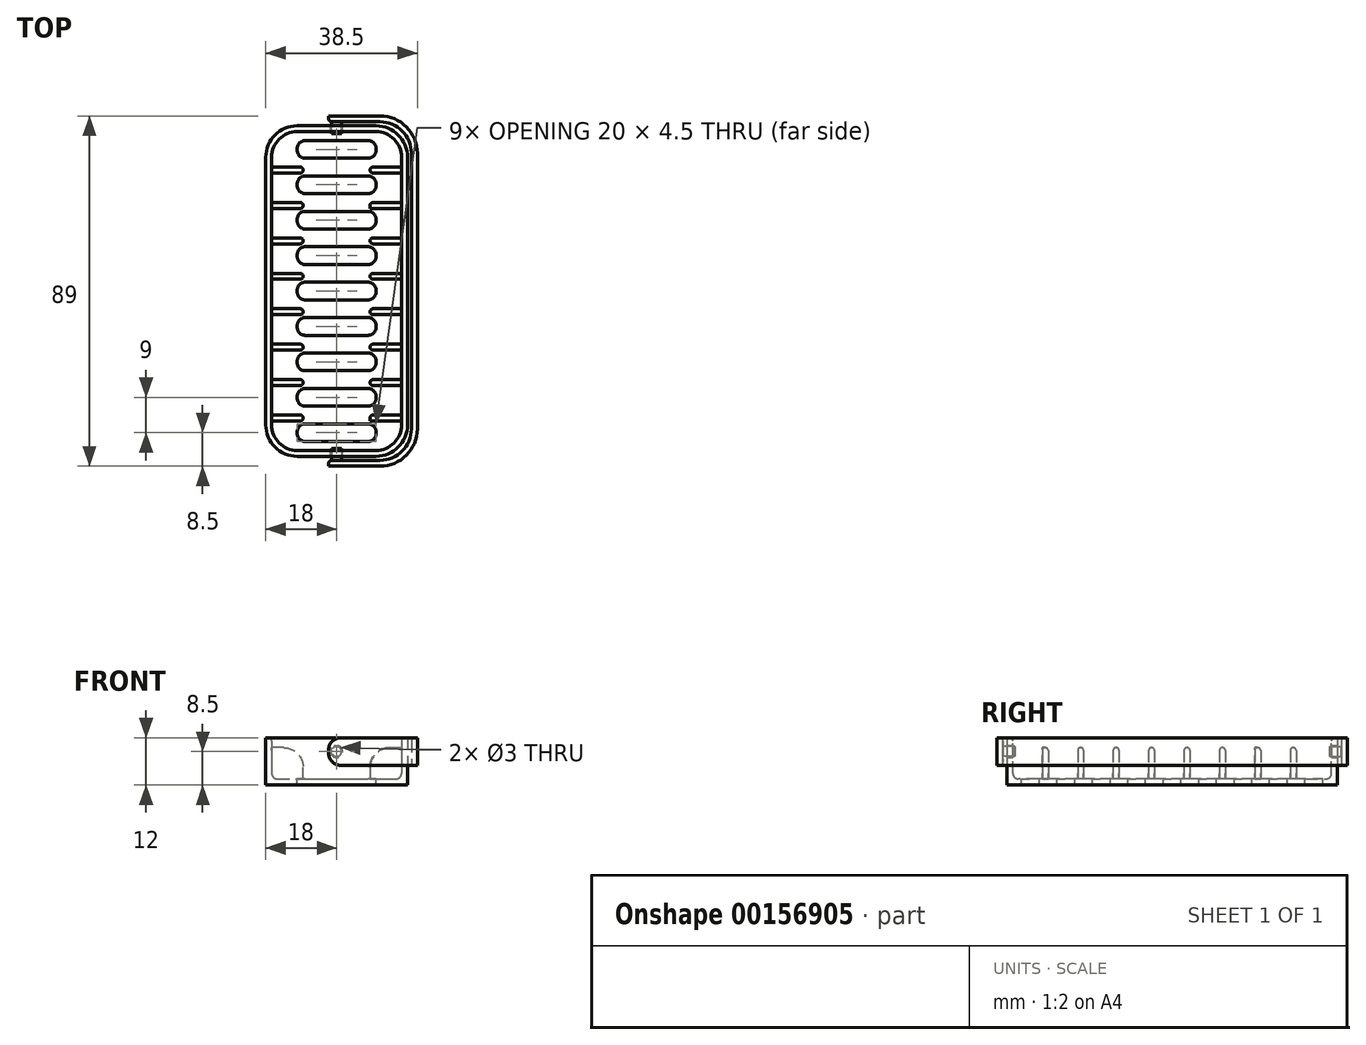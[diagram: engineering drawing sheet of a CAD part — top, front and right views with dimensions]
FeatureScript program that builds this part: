
annotation { "Feature Type Name" : "Feature", "Feature Type Description" : "" }
export const myFeature = defineFeature(function(context is Context, id is Id, definition is map)
    precondition{}
    {
        {
            var Q0;
            Q0=qCreatedBy(makeId("Top.planeOp"),FACE);
            var sketch = newSketch(context, id + "F0", { "sketchPlane" : qUnion([Q0])});
            skLineSegment(sketch, "E0.bottom", {"start": v(-18, 42) * mm, "end": v(18, 42) * mm});
            skLineSegment(sketch, "E0.top", {"start": v(-18, -42) * mm, "end": v(18, -42) * mm});
            skLineSegment(sketch, "E0.left", {"start": v(-18, 42) * mm, "end": v(-18, -42) * mm});
            skLineSegment(sketch, "E0.right", {"start": v(18, 42) * mm, "end": v(18, -42) * mm});
            skLineSegment(sketch, "E1", {"start": v(-18, 0) * mm, "end": v(18, 0) * mm, "construction": true});
            skSolve(sketch);
        }
        {
            var Q0;
            Q0=makeQuery(id+"F0.imprint","IMPRINT",FACE,{"disambiguationData":[TD([[makeQuery(id+"F0.imprint","IMPRINT",EDGE,{"derivedFrom":sQuery(id+"F0.wireOp",EDGE,"E0.bottom")}),-1.0]])]});
            extrude(context, id + "F1", {"entities" : qUnion([Q0]), "depth" : 12 * mm});
        }
        {
            var Q0;
            Q0=makeQuery(id+"F1.opExtrude","SWEPT_EDGE",EDGE,{"disambiguationData":[OSD([sQuery(id+"F0.wireOp",EDGE,"E0.bottom"),sQuery(id+"F0.wireOp",EDGE,"E0.right")])]});
            var Q1;
            Q1=makeQuery(id+"F1.opExtrude","SWEPT_EDGE",EDGE,{"disambiguationData":[OSD([sQuery(id+"F0.wireOp",EDGE,"E0.top"),sQuery(id+"F0.wireOp",EDGE,"E0.right")])]});
            var Q2;
            Q2=makeQuery(id+"F1.opExtrude","SWEPT_EDGE",EDGE,{"disambiguationData":[OSD([sQuery(id+"F0.wireOp",EDGE,"E0.top"),sQuery(id+"F0.wireOp",EDGE,"E0.left")])]});
            var Q3;
            Q3=makeQuery(id+"F1.opExtrude","SWEPT_EDGE",EDGE,{"disambiguationData":[OSD([sQuery(id+"F0.wireOp",EDGE,"E0.bottom"),sQuery(id+"F0.wireOp",EDGE,"E0.left")])]});
            fillet(context, id + "F2", {"entities" : qUnion([Q0, Q1, Q2, Q3]), "radius" : 8 * mm, "tangentPropagation" : true, "allowEdgeOverflow" : false});
        }
        {
            var Q0;
            Q0=makeQuery(id+"F1.opExtrude","CAP_FACE",FACE,{"disambiguationData":[OSD([sQuery(id+"F0.wireOp",EDGE,"E0.bottom"),sQuery(id+"F0.wireOp",EDGE,"E0.top"),sQuery(id+"F0.wireOp",EDGE,"E0.left"),sQuery(id+"F0.wireOp",EDGE,"E0.right")])],"isStart":false});
            var Q1;
            Q1=makeQuery(id+"F1.opExtrude","CAP_FACE",FACE,{"disambiguationData":[OSD([sQuery(id+"F0.wireOp",EDGE,"E0.bottom"),sQuery(id+"F0.wireOp",EDGE,"E0.top"),sQuery(id+"F0.wireOp",EDGE,"E0.left"),sQuery(id+"F0.wireOp",EDGE,"E0.right")])],"isStart":false});
            shell(context, id + "F3", {"entities" : qUnion([Q0, Q1]), "thickness" : 1.5 * mm});
        }
        {
            var Q0;
            Q0=makeQuery(id+"F3.opShell","OFFSET_FACE",FACE,{"disambiguationData":[OSD([sQuery(id+"F0.wireOp",EDGE,"E0.bottom"),sQuery(id+"F0.wireOp",EDGE,"E0.top"),sQuery(id+"F0.wireOp",EDGE,"E0.left"),sQuery(id+"F0.wireOp",EDGE,"E0.right")])]});
            var sketch = newSketch(context, id + "F4", { "sketchPlane" : qUnion([Q0])});
            skLineSegment(sketch, "E2.bottom", {"start": v(-16.5, 31.5) * mm, "end": v(-8.5, 31.5) * mm});
            skLineSegment(sketch, "E2.top", {"start": v(-16.5, 30) * mm, "end": v(-8.5, 30) * mm});
            skLineSegment(sketch, "E2.left", {"start": v(-16.5, 31.5) * mm, "end": v(-16.5, 30) * mm});
            skLineSegment(sketch, "E2.right", {"start": v(-8.5, 31.5) * mm, "end": v(-8.5, 30) * mm});
            skLineSegment(sketch, "E3.0.1.0", {"start": v(-16.5, 21) * mm, "end": v(-8.5, 21) * mm});
            skLineSegment(sketch, "E3.0.1.1", {"start": v(-16.5, 22.5) * mm, "end": v(-8.5, 22.5) * mm});
            skLineSegment(sketch, "E3.0.1.2", {"start": v(-8.5, 22.5) * mm, "end": v(-8.5, 21) * mm});
            skLineSegment(sketch, "E3.0.1.3", {"start": v(-16.5, 22.5) * mm, "end": v(-16.5, 21) * mm});
            skLineSegment(sketch, "E3.0.2.0", {"start": v(-16.5, 12) * mm, "end": v(-8.5, 12) * mm});
            skLineSegment(sketch, "E3.0.2.1", {"start": v(-16.5, 13.5) * mm, "end": v(-8.5, 13.5) * mm});
            skLineSegment(sketch, "E3.0.2.2", {"start": v(-8.5, 13.5) * mm, "end": v(-8.5, 12) * mm});
            skLineSegment(sketch, "E3.0.2.3", {"start": v(-16.5, 13.5) * mm, "end": v(-16.5, 12) * mm});
            skLineSegment(sketch, "E3.0.3.0", {"start": v(-16.5, 3) * mm, "end": v(-8.5, 3) * mm});
            skLineSegment(sketch, "E3.0.3.1", {"start": v(-16.5, 4.5) * mm, "end": v(-8.5, 4.5) * mm});
            skLineSegment(sketch, "E3.0.3.2", {"start": v(-8.5, 4.5) * mm, "end": v(-8.5, 3) * mm});
            skLineSegment(sketch, "E3.0.3.3", {"start": v(-16.5, 4.5) * mm, "end": v(-16.5, 3) * mm});
            skLineSegment(sketch, "E3.0.4.0", {"start": v(-16.5, -6) * mm, "end": v(-8.5, -6) * mm});
            skLineSegment(sketch, "E3.0.4.1", {"start": v(-16.5, -4.5) * mm, "end": v(-8.5, -4.5) * mm});
            skLineSegment(sketch, "E3.0.4.2", {"start": v(-8.5, -4.5) * mm, "end": v(-8.5, -6) * mm});
            skLineSegment(sketch, "E3.0.4.3", {"start": v(-16.5, -4.5) * mm, "end": v(-16.5, -6) * mm});
            skLineSegment(sketch, "E3.0.5.0", {"start": v(-16.5, -15) * mm, "end": v(-8.5, -15) * mm});
            skLineSegment(sketch, "E3.0.5.1", {"start": v(-16.5, -13.5) * mm, "end": v(-8.5, -13.5) * mm});
            skLineSegment(sketch, "E3.0.5.2", {"start": v(-8.5, -13.5) * mm, "end": v(-8.5, -15) * mm});
            skLineSegment(sketch, "E3.0.5.3", {"start": v(-16.5, -13.5) * mm, "end": v(-16.5, -15) * mm});
            skLineSegment(sketch, "E3.0.6.0", {"start": v(-16.5, -24) * mm, "end": v(-8.5, -24) * mm});
            skLineSegment(sketch, "E3.0.6.1", {"start": v(-16.5, -22.5) * mm, "end": v(-8.5, -22.5) * mm});
            skLineSegment(sketch, "E3.0.6.2", {"start": v(-8.5, -22.5) * mm, "end": v(-8.5, -24) * mm});
            skLineSegment(sketch, "E3.0.6.3", {"start": v(-16.5, -22.5) * mm, "end": v(-16.5, -24) * mm});
            skLineSegment(sketch, "E3.0.7.0", {"start": v(-16.5, -33) * mm, "end": v(-8.5, -33) * mm});
            skLineSegment(sketch, "E3.0.7.1", {"start": v(-16.5, -31.5) * mm, "end": v(-8.5, -31.5) * mm});
            skLineSegment(sketch, "E3.0.7.2", {"start": v(-8.5, -31.5) * mm, "end": v(-8.5, -33) * mm});
            skLineSegment(sketch, "E3.0.7.3", {"start": v(-16.5, -31.5) * mm, "end": v(-16.5, -33) * mm});
            skLineSegment(sketch, "E3.1.0.0", {"start": v(8.5, 30) * mm, "end": v(16.5, 30) * mm});
            skLineSegment(sketch, "E3.1.0.1", {"start": v(8.5, 31.5) * mm, "end": v(16.5, 31.5) * mm});
            skLineSegment(sketch, "E3.1.0.2", {"start": v(16.5, 31.5) * mm, "end": v(16.5, 30) * mm});
            skLineSegment(sketch, "E3.1.0.3", {"start": v(8.5, 31.5) * mm, "end": v(8.5, 30) * mm});
            skLineSegment(sketch, "E3.1.1.0", {"start": v(8.5, 21) * mm, "end": v(16.5, 21) * mm});
            skLineSegment(sketch, "E3.1.1.1", {"start": v(8.5, 22.5) * mm, "end": v(16.5, 22.5) * mm});
            skLineSegment(sketch, "E3.1.1.2", {"start": v(16.5, 22.5) * mm, "end": v(16.5, 21) * mm});
            skLineSegment(sketch, "E3.1.1.3", {"start": v(8.5, 22.5) * mm, "end": v(8.5, 21) * mm});
            skLineSegment(sketch, "E3.1.2.0", {"start": v(8.5, 12) * mm, "end": v(16.5, 12) * mm});
            skLineSegment(sketch, "E3.1.2.1", {"start": v(8.5, 13.5) * mm, "end": v(16.5, 13.5) * mm});
            skLineSegment(sketch, "E3.1.2.2", {"start": v(16.5, 13.5) * mm, "end": v(16.5, 12) * mm});
            skLineSegment(sketch, "E3.1.2.3", {"start": v(8.5, 13.5) * mm, "end": v(8.5, 12) * mm});
            skLineSegment(sketch, "E3.1.3.0", {"start": v(8.5, 3) * mm, "end": v(16.5, 3) * mm});
            skLineSegment(sketch, "E3.1.3.1", {"start": v(8.5, 4.5) * mm, "end": v(16.5, 4.5) * mm});
            skLineSegment(sketch, "E3.1.3.2", {"start": v(16.5, 4.5) * mm, "end": v(16.5, 3) * mm});
            skLineSegment(sketch, "E3.1.3.3", {"start": v(8.5, 4.5) * mm, "end": v(8.5, 3) * mm});
            skLineSegment(sketch, "E3.1.4.0", {"start": v(8.5, -6) * mm, "end": v(16.5, -6) * mm});
            skLineSegment(sketch, "E3.1.4.1", {"start": v(8.5, -4.5) * mm, "end": v(16.5, -4.5) * mm});
            skLineSegment(sketch, "E3.1.4.2", {"start": v(16.5, -4.5) * mm, "end": v(16.5, -6) * mm});
            skLineSegment(sketch, "E3.1.4.3", {"start": v(8.5, -4.5) * mm, "end": v(8.5, -6) * mm});
            skLineSegment(sketch, "E3.1.5.0", {"start": v(8.5, -15) * mm, "end": v(16.5, -15) * mm});
            skLineSegment(sketch, "E3.1.5.1", {"start": v(8.5, -13.5) * mm, "end": v(16.5, -13.5) * mm});
            skLineSegment(sketch, "E3.1.5.2", {"start": v(16.5, -13.5) * mm, "end": v(16.5, -15) * mm});
            skLineSegment(sketch, "E3.1.5.3", {"start": v(8.5, -13.5) * mm, "end": v(8.5, -15) * mm});
            skLineSegment(sketch, "E3.1.6.0", {"start": v(8.5, -24) * mm, "end": v(16.5, -24) * mm});
            skLineSegment(sketch, "E3.1.6.1", {"start": v(8.5, -22.5) * mm, "end": v(16.5, -22.5) * mm});
            skLineSegment(sketch, "E3.1.6.2", {"start": v(16.5, -22.5) * mm, "end": v(16.5, -24) * mm});
            skLineSegment(sketch, "E3.1.6.3", {"start": v(8.5, -22.5) * mm, "end": v(8.5, -24) * mm});
            skLineSegment(sketch, "E3.1.7.0", {"start": v(8.5, -33) * mm, "end": v(16.5, -33) * mm});
            skLineSegment(sketch, "E3.1.7.1", {"start": v(8.5, -31.5) * mm, "end": v(16.5, -31.5) * mm});
            skLineSegment(sketch, "E3.1.7.2", {"start": v(16.5, -31.5) * mm, "end": v(16.5, -33) * mm});
            skLineSegment(sketch, "E3.1.7.3", {"start": v(8.5, -31.5) * mm, "end": v(8.5, -33) * mm});
            skLineSegment(sketch, "E3.direction1", {"start": v(-16.5, 30) * mm, "end": v(8.5, 30) * mm, "construction": true});
            skLineSegment(sketch, "E3.direction2", {"start": v(-16.5, 30) * mm, "end": v(-16.5, 21) * mm, "construction": true});
            skSolve(sketch);
        }
        {
            var Q0;
            Q0 = qSketchRegion(id + "F4", true);
            extrude(context, id + "F5", {"entities" : qUnion([Q0]), "operationType" : NewBodyOperationType.ADD, "depth" : 8 * mm});
        }
        {
            var Q0;
            Q0=makeQuery(id+"F5.opExtrude","CAP_EDGE",EDGE,{"disambiguationData":[OSD([sQuery(id+"F4.wireOp",EDGE,"E3.0.7.2")])],"isStart":false});
            var Q1;
            Q1=makeQuery(id+"F5.opExtrude","CAP_EDGE",EDGE,{"disambiguationData":[OSD([sQuery(id+"F4.wireOp",EDGE,"E3.0.6.2")])],"isStart":false});
            var Q2;
            Q2=makeQuery(id+"F5.opExtrude","CAP_EDGE",EDGE,{"disambiguationData":[OSD([sQuery(id+"F4.wireOp",EDGE,"E3.0.5.2")])],"isStart":false});
            var Q3;
            Q3=makeQuery(id+"F5.opExtrude","CAP_EDGE",EDGE,{"disambiguationData":[OSD([sQuery(id+"F4.wireOp",EDGE,"E3.0.4.2")])],"isStart":false});
            var Q4;
            Q4=makeQuery(id+"F5.opExtrude","CAP_EDGE",EDGE,{"disambiguationData":[OSD([sQuery(id+"F4.wireOp",EDGE,"E3.0.3.2")])],"isStart":false});
            var Q5;
            Q5=makeQuery(id+"F5.opExtrude","CAP_EDGE",EDGE,{"disambiguationData":[OSD([sQuery(id+"F4.wireOp",EDGE,"E3.0.2.2")])],"isStart":false});
            var Q6;
            Q6=makeQuery(id+"F5.opExtrude","CAP_EDGE",EDGE,{"disambiguationData":[OSD([sQuery(id+"F4.wireOp",EDGE,"E3.0.1.2")])],"isStart":false});
            var Q7;
            Q7=makeQuery(id+"F5.opExtrude","CAP_EDGE",EDGE,{"disambiguationData":[OSD([sQuery(id+"F4.wireOp",EDGE,"E2.right")])],"isStart":false});
            var Q8;
            Q8=makeQuery(id+"F5.opExtrude","CAP_EDGE",EDGE,{"disambiguationData":[OSD([sQuery(id+"F4.wireOp",EDGE,"E3.1.0.3")])],"isStart":false});
            var Q9;
            Q9=makeQuery(id+"F5.opExtrude","CAP_EDGE",EDGE,{"disambiguationData":[OSD([sQuery(id+"F4.wireOp",EDGE,"E3.1.1.3")])],"isStart":false});
            var Q10;
            Q10=makeQuery(id+"F5.opExtrude","CAP_EDGE",EDGE,{"disambiguationData":[OSD([sQuery(id+"F4.wireOp",EDGE,"E3.1.2.3")])],"isStart":false});
            var Q11;
            Q11=makeQuery(id+"F5.opExtrude","CAP_EDGE",EDGE,{"disambiguationData":[OSD([sQuery(id+"F4.wireOp",EDGE,"E3.1.3.3")])],"isStart":false});
            var Q12;
            Q12=makeQuery(id+"F5.opExtrude","CAP_EDGE",EDGE,{"disambiguationData":[OSD([sQuery(id+"F4.wireOp",EDGE,"E3.1.4.3")])],"isStart":false});
            var Q13;
            Q13=makeQuery(id+"F5.opExtrude","CAP_EDGE",EDGE,{"disambiguationData":[OSD([sQuery(id+"F4.wireOp",EDGE,"E3.1.5.3")])],"isStart":false});
            var Q14;
            Q14=makeQuery(id+"F5.opExtrude","CAP_EDGE",EDGE,{"disambiguationData":[OSD([sQuery(id+"F4.wireOp",EDGE,"E3.1.6.3")])],"isStart":false});
            var Q15;
            Q15=makeQuery(id+"F5.opExtrude","CAP_EDGE",EDGE,{"disambiguationData":[OSD([sQuery(id+"F4.wireOp",EDGE,"E3.1.7.3")])],"isStart":false});
            fillet(context, id + "F6", {"entities" : qUnion([Q0, Q1, Q2, Q3, Q4, Q5, Q6, Q7, Q8, Q9, Q10, Q11, Q12, Q13, Q14, Q15]), "radius" : 5 * mm, "tangentPropagation" : true, "allowEdgeOverflow" : false});
        }
        {
            var Q0;
            Q0=makeQuery(id+"F3.opShell","OFFSET_FACE",FACE,{"disambiguationData":[OSD([sQuery(id+"F0.wireOp",EDGE,"E0.bottom"),sQuery(id+"F0.wireOp",EDGE,"E0.top"),sQuery(id+"F0.wireOp",EDGE,"E0.left"),sQuery(id+"F0.wireOp",EDGE,"E0.right")])]});
            var sketch = newSketch(context, id + "F7", { "sketchPlane" : qUnion([Q0])});
            skLineSegment(sketch, "E4.bottom", {"start": v(-10, 38.25) * mm, "end": v(10, 38.25) * mm});
            skLineSegment(sketch, "E4.top", {"start": v(-10, 33.75) * mm, "end": v(10, 33.75) * mm});
            skLineSegment(sketch, "E4.left", {"start": v(-10, 38.25) * mm, "end": v(-10, 33.75) * mm});
            skLineSegment(sketch, "E4.right", {"start": v(10, 38.25) * mm, "end": v(10, 33.75) * mm});
            skLineSegment(sketch, "E5", {"start": v(0, 33.75) * mm, "end": v(0, 0) * mm, "construction": true});
            skLineSegment(sketch, "E6", {"start": v(-10, 36) * mm, "end": v(10, 36) * mm, "construction": true});
            skLineSegment(sketch, "E7.0.1.0", {"start": v(-10, 29.25) * mm, "end": v(10, 29.25) * mm});
            skLineSegment(sketch, "E7.0.1.1", {"start": v(10, 29.25) * mm, "end": v(10, 24.75) * mm});
            skLineSegment(sketch, "E7.0.1.2", {"start": v(-10, 24.75) * mm, "end": v(10, 24.75) * mm});
            skLineSegment(sketch, "E7.0.1.3", {"start": v(-10, 29.25) * mm, "end": v(-10, 24.75) * mm});
            skLineSegment(sketch, "E7.0.2.0", {"start": v(-10, 20.25) * mm, "end": v(10, 20.25) * mm});
            skLineSegment(sketch, "E7.0.2.1", {"start": v(10, 20.25) * mm, "end": v(10, 15.75) * mm});
            skLineSegment(sketch, "E7.0.2.2", {"start": v(-10, 15.75) * mm, "end": v(10, 15.75) * mm});
            skLineSegment(sketch, "E7.0.2.3", {"start": v(-10, 20.25) * mm, "end": v(-10, 15.75) * mm});
            skLineSegment(sketch, "E7.0.3.0", {"start": v(-10, 11.25) * mm, "end": v(10, 11.25) * mm});
            skLineSegment(sketch, "E7.0.3.1", {"start": v(10, 11.25) * mm, "end": v(10, 6.75) * mm});
            skLineSegment(sketch, "E7.0.3.2", {"start": v(-10, 6.75) * mm, "end": v(10, 6.75) * mm});
            skLineSegment(sketch, "E7.0.3.3", {"start": v(-10, 11.25) * mm, "end": v(-10, 6.75) * mm});
            skLineSegment(sketch, "E7.0.4.0", {"start": v(-10, 2.25) * mm, "end": v(10, 2.25) * mm});
            skLineSegment(sketch, "E7.0.4.1", {"start": v(10, 2.25) * mm, "end": v(10, -2.25) * mm});
            skLineSegment(sketch, "E7.0.4.2", {"start": v(-10, -2.25) * mm, "end": v(10, -2.25) * mm});
            skLineSegment(sketch, "E7.0.4.3", {"start": v(-10, 2.25) * mm, "end": v(-10, -2.25) * mm});
            skLineSegment(sketch, "E7.0.5.0", {"start": v(-10, -6.75) * mm, "end": v(10, -6.75) * mm});
            skLineSegment(sketch, "E7.0.5.1", {"start": v(10, -6.75) * mm, "end": v(10, -11.25) * mm});
            skLineSegment(sketch, "E7.0.5.2", {"start": v(-10, -11.25) * mm, "end": v(10, -11.25) * mm});
            skLineSegment(sketch, "E7.0.5.3", {"start": v(-10, -6.75) * mm, "end": v(-10, -11.25) * mm});
            skLineSegment(sketch, "E7.0.6.0", {"start": v(-10, -15.75) * mm, "end": v(10, -15.75) * mm});
            skLineSegment(sketch, "E7.0.6.1", {"start": v(10, -15.75) * mm, "end": v(10, -20.25) * mm});
            skLineSegment(sketch, "E7.0.6.2", {"start": v(-10, -20.25) * mm, "end": v(10, -20.25) * mm});
            skLineSegment(sketch, "E7.0.6.3", {"start": v(-10, -15.75) * mm, "end": v(-10, -20.25) * mm});
            skLineSegment(sketch, "E7.0.7.0", {"start": v(-10, -24.75) * mm, "end": v(10, -24.75) * mm});
            skLineSegment(sketch, "E7.0.7.1", {"start": v(10, -24.75) * mm, "end": v(10, -29.25) * mm});
            skLineSegment(sketch, "E7.0.7.2", {"start": v(-10, -29.25) * mm, "end": v(10, -29.25) * mm});
            skLineSegment(sketch, "E7.0.7.3", {"start": v(-10, -24.75) * mm, "end": v(-10, -29.25) * mm});
            skLineSegment(sketch, "E7.0.8.0", {"start": v(-10, -33.75) * mm, "end": v(10, -33.75) * mm});
            skLineSegment(sketch, "E7.0.8.1", {"start": v(10, -33.75) * mm, "end": v(10, -38.25) * mm});
            skLineSegment(sketch, "E7.0.8.2", {"start": v(-10, -38.25) * mm, "end": v(10, -38.25) * mm});
            skLineSegment(sketch, "E7.0.8.3", {"start": v(-10, -33.75) * mm, "end": v(-10, -38.25) * mm});
            skLineSegment(sketch, "E7.direction1", {"start": v(-10, 33.75) * mm, "end": v(15, 33.75) * mm, "construction": true});
            skLineSegment(sketch, "E7.direction2", {"start": v(-10, 33.75) * mm, "end": v(-10, 24.75) * mm, "construction": true});
            skSolve(sketch);
        }
        {
            var Q0;
            Q0 = qSketchRegion(id + "F7", true);
            extrude(context, id + "F8", {"entities" : qUnion([Q0]), "operationType" : NewBodyOperationType.REMOVE, "oppositeDirection" : true, "depth" : 25 * mm});
        }
        {
            var Q0;
            Q0=makeQuery(id+"F8.boolean.opBoolean","COPY",EDGE,{"derivedFrom":makeQuery(id+"F8.opExtrude","SWEPT_EDGE",EDGE,{"disambiguationData":[OSD([sQuery(id+"F7.wireOp",EDGE,"E4.bottom"),sQuery(id+"F7.wireOp",EDGE,"E4.left")])]})});
            var Q1;
            Q1=makeQuery(id+"F8.boolean.opBoolean","COPY",EDGE,{"derivedFrom":makeQuery(id+"F8.opExtrude","SWEPT_EDGE",EDGE,{"disambiguationData":[OSD([sQuery(id+"F7.wireOp",EDGE,"E4.bottom"),sQuery(id+"F7.wireOp",EDGE,"E4.right")])]})});
            var Q2;
            Q2=makeQuery(id+"F8.boolean.opBoolean","COPY",EDGE,{"derivedFrom":makeQuery(id+"F8.opExtrude","SWEPT_EDGE",EDGE,{"disambiguationData":[OSD([sQuery(id+"F7.wireOp",EDGE,"E7.0.1.0"),sQuery(id+"F7.wireOp",EDGE,"E7.0.1.1")])]})});
            var Q3;
            Q3=makeQuery(id+"F8.boolean.opBoolean","COPY",EDGE,{"derivedFrom":makeQuery(id+"F8.opExtrude","SWEPT_EDGE",EDGE,{"disambiguationData":[OSD([sQuery(id+"F7.wireOp",EDGE,"E7.0.2.0"),sQuery(id+"F7.wireOp",EDGE,"E7.0.2.1")])]})});
            var Q4;
            Q4=makeQuery(id+"F8.boolean.opBoolean","COPY",EDGE,{"derivedFrom":makeQuery(id+"F8.opExtrude","SWEPT_EDGE",EDGE,{"disambiguationData":[OSD([sQuery(id+"F7.wireOp",EDGE,"E7.0.3.0"),sQuery(id+"F7.wireOp",EDGE,"E7.0.3.1")])]})});
            var Q5;
            Q5=makeQuery(id+"F8.boolean.opBoolean","COPY",EDGE,{"derivedFrom":makeQuery(id+"F8.opExtrude","SWEPT_EDGE",EDGE,{"disambiguationData":[OSD([sQuery(id+"F7.wireOp",EDGE,"E7.0.4.0"),sQuery(id+"F7.wireOp",EDGE,"E7.0.4.1")])]})});
            var Q6;
            Q6=makeQuery(id+"F8.boolean.opBoolean","COPY",EDGE,{"derivedFrom":makeQuery(id+"F8.opExtrude","SWEPT_EDGE",EDGE,{"disambiguationData":[OSD([sQuery(id+"F7.wireOp",EDGE,"E7.0.5.0"),sQuery(id+"F7.wireOp",EDGE,"E7.0.5.1")])]})});
            var Q7;
            Q7=makeQuery(id+"F8.boolean.opBoolean","COPY",EDGE,{"derivedFrom":makeQuery(id+"F8.opExtrude","SWEPT_EDGE",EDGE,{"disambiguationData":[OSD([sQuery(id+"F7.wireOp",EDGE,"E7.0.6.0"),sQuery(id+"F7.wireOp",EDGE,"E7.0.6.1")])]})});
            var Q8;
            Q8=makeQuery(id+"F8.boolean.opBoolean","COPY",EDGE,{"derivedFrom":makeQuery(id+"F8.opExtrude","SWEPT_EDGE",EDGE,{"disambiguationData":[OSD([sQuery(id+"F7.wireOp",EDGE,"E7.0.7.0"),sQuery(id+"F7.wireOp",EDGE,"E7.0.7.1")])]})});
            var Q9;
            Q9=makeQuery(id+"F8.boolean.opBoolean","COPY",EDGE,{"derivedFrom":makeQuery(id+"F8.opExtrude","SWEPT_EDGE",EDGE,{"disambiguationData":[OSD([sQuery(id+"F7.wireOp",EDGE,"E7.0.8.1"),sQuery(id+"F7.wireOp",EDGE,"E7.0.8.2")])]})});
            var Q10;
            Q10=makeQuery(id+"F8.boolean.opBoolean","COPY",EDGE,{"derivedFrom":makeQuery(id+"F8.opExtrude","SWEPT_EDGE",EDGE,{"disambiguationData":[OSD([sQuery(id+"F7.wireOp",EDGE,"E7.0.7.1"),sQuery(id+"F7.wireOp",EDGE,"E7.0.7.2")])]})});
            var Q11;
            Q11=makeQuery(id+"F8.boolean.opBoolean","COPY",EDGE,{"derivedFrom":makeQuery(id+"F8.opExtrude","SWEPT_EDGE",EDGE,{"disambiguationData":[OSD([sQuery(id+"F7.wireOp",EDGE,"E7.0.6.1"),sQuery(id+"F7.wireOp",EDGE,"E7.0.6.2")])]})});
            var Q12;
            Q12=makeQuery(id+"F8.boolean.opBoolean","COPY",EDGE,{"derivedFrom":makeQuery(id+"F8.opExtrude","SWEPT_EDGE",EDGE,{"disambiguationData":[OSD([sQuery(id+"F7.wireOp",EDGE,"E7.0.5.1"),sQuery(id+"F7.wireOp",EDGE,"E7.0.5.2")])]})});
            var Q13;
            Q13=makeQuery(id+"F8.boolean.opBoolean","COPY",EDGE,{"derivedFrom":makeQuery(id+"F8.opExtrude","SWEPT_EDGE",EDGE,{"disambiguationData":[OSD([sQuery(id+"F7.wireOp",EDGE,"E7.0.4.1"),sQuery(id+"F7.wireOp",EDGE,"E7.0.4.2")])]})});
            var Q14;
            Q14=makeQuery(id+"F8.boolean.opBoolean","COPY",EDGE,{"derivedFrom":makeQuery(id+"F8.opExtrude","SWEPT_EDGE",EDGE,{"disambiguationData":[OSD([sQuery(id+"F7.wireOp",EDGE,"E7.0.3.1"),sQuery(id+"F7.wireOp",EDGE,"E7.0.3.2")])]})});
            var Q15;
            Q15=makeQuery(id+"F8.boolean.opBoolean","COPY",EDGE,{"derivedFrom":makeQuery(id+"F8.opExtrude","SWEPT_EDGE",EDGE,{"disambiguationData":[OSD([sQuery(id+"F7.wireOp",EDGE,"E7.0.2.1"),sQuery(id+"F7.wireOp",EDGE,"E7.0.2.2")])]})});
            var Q16;
            Q16=makeQuery(id+"F8.boolean.opBoolean","COPY",EDGE,{"derivedFrom":makeQuery(id+"F8.opExtrude","SWEPT_EDGE",EDGE,{"disambiguationData":[OSD([sQuery(id+"F7.wireOp",EDGE,"E4.top"),sQuery(id+"F7.wireOp",EDGE,"E4.right")])]})});
            var Q17;
            Q17=makeQuery(id+"F8.boolean.opBoolean","COPY",EDGE,{"derivedFrom":makeQuery(id+"F8.opExtrude","SWEPT_EDGE",EDGE,{"disambiguationData":[OSD([sQuery(id+"F7.wireOp",EDGE,"E7.0.1.1"),sQuery(id+"F7.wireOp",EDGE,"E7.0.1.2")])]})});
            var Q18;
            Q18=makeQuery(id+"F8.boolean.opBoolean","COPY",EDGE,{"derivedFrom":makeQuery(id+"F8.opExtrude","SWEPT_EDGE",EDGE,{"disambiguationData":[OSD([sQuery(id+"F7.wireOp",EDGE,"E7.0.2.0"),sQuery(id+"F7.wireOp",EDGE,"E7.0.2.3")])]})});
            var Q19;
            Q19=makeQuery(id+"F8.boolean.opBoolean","COPY",EDGE,{"derivedFrom":makeQuery(id+"F8.opExtrude","SWEPT_EDGE",EDGE,{"disambiguationData":[OSD([sQuery(id+"F7.wireOp",EDGE,"E7.0.1.0"),sQuery(id+"F7.wireOp",EDGE,"E7.0.1.3")])]})});
            var Q20;
            Q20=makeQuery(id+"F8.boolean.opBoolean","COPY",EDGE,{"derivedFrom":makeQuery(id+"F8.opExtrude","SWEPT_EDGE",EDGE,{"disambiguationData":[OSD([sQuery(id+"F7.wireOp",EDGE,"E7.0.3.0"),sQuery(id+"F7.wireOp",EDGE,"E7.0.3.3")])]})});
            var Q21;
            Q21=makeQuery(id+"F8.boolean.opBoolean","COPY",EDGE,{"derivedFrom":makeQuery(id+"F8.opExtrude","SWEPT_EDGE",EDGE,{"disambiguationData":[OSD([sQuery(id+"F7.wireOp",EDGE,"E7.0.4.0"),sQuery(id+"F7.wireOp",EDGE,"E7.0.4.3")])]})});
            var Q22;
            Q22=makeQuery(id+"F8.boolean.opBoolean","COPY",EDGE,{"derivedFrom":makeQuery(id+"F8.opExtrude","SWEPT_EDGE",EDGE,{"disambiguationData":[OSD([sQuery(id+"F7.wireOp",EDGE,"E7.0.5.0"),sQuery(id+"F7.wireOp",EDGE,"E7.0.5.3")])]})});
            var Q23;
            Q23=makeQuery(id+"F8.boolean.opBoolean","COPY",EDGE,{"derivedFrom":makeQuery(id+"F8.opExtrude","SWEPT_EDGE",EDGE,{"disambiguationData":[OSD([sQuery(id+"F7.wireOp",EDGE,"E7.0.6.0"),sQuery(id+"F7.wireOp",EDGE,"E7.0.6.3")])]})});
            var Q24;
            Q24=makeQuery(id+"F8.boolean.opBoolean","COPY",EDGE,{"derivedFrom":makeQuery(id+"F8.opExtrude","SWEPT_EDGE",EDGE,{"disambiguationData":[OSD([sQuery(id+"F7.wireOp",EDGE,"E7.0.6.2"),sQuery(id+"F7.wireOp",EDGE,"E7.0.6.3")])]})});
            var Q25;
            Q25=makeQuery(id+"F8.boolean.opBoolean","COPY",EDGE,{"derivedFrom":makeQuery(id+"F8.opExtrude","SWEPT_EDGE",EDGE,{"disambiguationData":[OSD([sQuery(id+"F7.wireOp",EDGE,"E7.0.7.2"),sQuery(id+"F7.wireOp",EDGE,"E7.0.7.3")])]})});
            var Q26;
            Q26=makeQuery(id+"F8.boolean.opBoolean","COPY",EDGE,{"derivedFrom":makeQuery(id+"F8.opExtrude","SWEPT_EDGE",EDGE,{"disambiguationData":[OSD([sQuery(id+"F7.wireOp",EDGE,"E7.0.8.2"),sQuery(id+"F7.wireOp",EDGE,"E7.0.8.3")])]})});
            var Q27;
            Q27=makeQuery(id+"F8.boolean.opBoolean","COPY",EDGE,{"derivedFrom":makeQuery(id+"F8.opExtrude","SWEPT_EDGE",EDGE,{"disambiguationData":[OSD([sQuery(id+"F7.wireOp",EDGE,"E7.0.5.2"),sQuery(id+"F7.wireOp",EDGE,"E7.0.5.3")])]})});
            var Q28;
            Q28=makeQuery(id+"F8.boolean.opBoolean","COPY",EDGE,{"derivedFrom":makeQuery(id+"F8.opExtrude","SWEPT_EDGE",EDGE,{"disambiguationData":[OSD([sQuery(id+"F7.wireOp",EDGE,"E7.0.4.2"),sQuery(id+"F7.wireOp",EDGE,"E7.0.4.3")])]})});
            var Q29;
            Q29=makeQuery(id+"F8.boolean.opBoolean","COPY",EDGE,{"derivedFrom":makeQuery(id+"F8.opExtrude","SWEPT_EDGE",EDGE,{"disambiguationData":[OSD([sQuery(id+"F7.wireOp",EDGE,"E7.0.8.0"),sQuery(id+"F7.wireOp",EDGE,"E7.0.8.3")])]})});
            var Q30;
            Q30=makeQuery(id+"F8.boolean.opBoolean","COPY",EDGE,{"derivedFrom":makeQuery(id+"F8.opExtrude","SWEPT_EDGE",EDGE,{"disambiguationData":[OSD([sQuery(id+"F7.wireOp",EDGE,"E7.0.7.0"),sQuery(id+"F7.wireOp",EDGE,"E7.0.7.3")])]})});
            var Q31;
            Q31=makeQuery(id+"F8.boolean.opBoolean","COPY",EDGE,{"derivedFrom":makeQuery(id+"F8.opExtrude","SWEPT_EDGE",EDGE,{"disambiguationData":[OSD([sQuery(id+"F7.wireOp",EDGE,"E7.0.3.2"),sQuery(id+"F7.wireOp",EDGE,"E7.0.3.3")])]})});
            var Q32;
            Q32=makeQuery(id+"F8.boolean.opBoolean","COPY",EDGE,{"derivedFrom":makeQuery(id+"F8.opExtrude","SWEPT_EDGE",EDGE,{"disambiguationData":[OSD([sQuery(id+"F7.wireOp",EDGE,"E7.0.2.2"),sQuery(id+"F7.wireOp",EDGE,"E7.0.2.3")])]})});
            var Q33;
            Q33=makeQuery(id+"F8.boolean.opBoolean","COPY",EDGE,{"derivedFrom":makeQuery(id+"F8.opExtrude","SWEPT_EDGE",EDGE,{"disambiguationData":[OSD([sQuery(id+"F7.wireOp",EDGE,"E7.0.1.2"),sQuery(id+"F7.wireOp",EDGE,"E7.0.1.3")])]})});
            var Q34;
            Q34=makeQuery(id+"F8.boolean.opBoolean","COPY",EDGE,{"derivedFrom":makeQuery(id+"F8.opExtrude","SWEPT_EDGE",EDGE,{"disambiguationData":[OSD([sQuery(id+"F7.wireOp",EDGE,"E4.top"),sQuery(id+"F7.wireOp",EDGE,"E4.left")])]})});
            var Q35;
            Q35=makeQuery(id+"F8.boolean.opBoolean","COPY",EDGE,{"derivedFrom":makeQuery(id+"F8.opExtrude","SWEPT_EDGE",EDGE,{"disambiguationData":[OSD([sQuery(id+"F7.wireOp",EDGE,"E7.0.8.0"),sQuery(id+"F7.wireOp",EDGE,"E7.0.8.1")])]})});
            fillet(context, id + "F9", {"entities" : qUnion([Q0, Q1, Q2, Q3, Q4, Q5, Q6, Q7, Q8, Q9, Q10, Q11, Q12, Q13, Q14, Q15, Q16, Q17, Q18, Q19, Q20, Q21, Q22, Q23, Q24, Q25, Q26, Q27, Q28, Q29, Q30, Q31, Q32, Q33, Q34, Q35]), "radius" : 2 * mm, "tangentPropagation" : true, "allowEdgeOverflow" : false});
        }
        {
            var Q0;
            {var subQ0=sQuery(id+"F0.wireOp",EDGE,"E0.right");Q0=makeQuery(id+"F5.boolean.opBoolean","SPLIT",EDGE,{"disambiguationData":[TD([makeQuery(id+"F5.opExtrude","SWEPT_FACE",FACE,{"disambiguationData":[OSD([sQuery(id+"F4.wireOp",EDGE,"E3.1.0.0")])]})])],"derivedFrom":makeQuery(id+"F3.opShell","OFFSET_EDGE",EDGE,{"disambiguationData":[OSD([subQ0]),TDD([makeQuery(id+"F1.opExtrude","CAP_EDGE",EDGE,{"disambiguationData":[OSD([subQ0])],"isStart":true})])]})});}
            var Q1;
            {var subQ0=sQuery(id+"F0.wireOp",EDGE,"E0.right");Q1=makeQuery(id+"F5.boolean.opBoolean","SPLIT",EDGE,{"disambiguationData":[TD([makeQuery(id+"F5.opExtrude","SWEPT_FACE",FACE,{"disambiguationData":[OSD([sQuery(id+"F4.wireOp",EDGE,"E3.1.1.0")])]})])],"derivedFrom":makeQuery(id+"F3.opShell","OFFSET_EDGE",EDGE,{"disambiguationData":[OSD([subQ0]),TDD([makeQuery(id+"F1.opExtrude","CAP_EDGE",EDGE,{"disambiguationData":[OSD([subQ0])],"isStart":true})])]})});}
            var Q2;
            {var subQ0=sQuery(id+"F0.wireOp",EDGE,"E0.right");Q2=makeQuery(id+"F5.boolean.opBoolean","SPLIT",EDGE,{"disambiguationData":[TD([makeQuery(id+"F5.opExtrude","SWEPT_FACE",FACE,{"disambiguationData":[OSD([sQuery(id+"F4.wireOp",EDGE,"E3.1.2.0")])]})])],"derivedFrom":makeQuery(id+"F3.opShell","OFFSET_EDGE",EDGE,{"disambiguationData":[OSD([subQ0]),TDD([makeQuery(id+"F1.opExtrude","CAP_EDGE",EDGE,{"disambiguationData":[OSD([subQ0])],"isStart":true})])]})});}
            var Q3;
            {var subQ0=sQuery(id+"F0.wireOp",EDGE,"E0.right");Q3=makeQuery(id+"F5.boolean.opBoolean","SPLIT",EDGE,{"disambiguationData":[TD([makeQuery(id+"F5.opExtrude","SWEPT_FACE",FACE,{"disambiguationData":[OSD([sQuery(id+"F4.wireOp",EDGE,"E3.1.3.0")])]})])],"derivedFrom":makeQuery(id+"F3.opShell","OFFSET_EDGE",EDGE,{"disambiguationData":[OSD([subQ0]),TDD([makeQuery(id+"F1.opExtrude","CAP_EDGE",EDGE,{"disambiguationData":[OSD([subQ0])],"isStart":true})])]})});}
            var Q4;
            {var subQ0=sQuery(id+"F0.wireOp",EDGE,"E0.right");Q4=makeQuery(id+"F5.boolean.opBoolean","SPLIT",EDGE,{"disambiguationData":[TD([makeQuery(id+"F5.opExtrude","SWEPT_FACE",FACE,{"disambiguationData":[OSD([sQuery(id+"F4.wireOp",EDGE,"E3.1.4.0")])]})])],"derivedFrom":makeQuery(id+"F3.opShell","OFFSET_EDGE",EDGE,{"disambiguationData":[OSD([subQ0]),TDD([makeQuery(id+"F1.opExtrude","CAP_EDGE",EDGE,{"disambiguationData":[OSD([subQ0])],"isStart":true})])]})});}
            var Q5;
            {var subQ0=sQuery(id+"F0.wireOp",EDGE,"E0.right");Q5=makeQuery(id+"F5.boolean.opBoolean","SPLIT",EDGE,{"disambiguationData":[TD([makeQuery(id+"F5.opExtrude","SWEPT_FACE",FACE,{"disambiguationData":[OSD([sQuery(id+"F4.wireOp",EDGE,"E3.1.5.0")])]})])],"derivedFrom":makeQuery(id+"F3.opShell","OFFSET_EDGE",EDGE,{"disambiguationData":[OSD([subQ0]),TDD([makeQuery(id+"F1.opExtrude","CAP_EDGE",EDGE,{"disambiguationData":[OSD([subQ0])],"isStart":true})])]})});}
            var Q6;
            {var subQ0=sQuery(id+"F0.wireOp",EDGE,"E0.right");var subQ1=sQuery(id+"F0.wireOp",EDGE,"E0.left");var subQ2=sQuery(id+"F0.wireOp",EDGE,"E0.top");var subQ3=sQuery(id+"F0.wireOp",EDGE,"E0.bottom");Q6=makeQuery(id+"F3.opShell","OFFSET_EDGE",EDGE,{"disambiguationData":[OSD([subQ3,subQ2,subQ1,subQ0]),TDD([makeQuery(id+"F2.opFillet","BLEND_EDGE",EDGE,{"blendedFrom":[makeQuery(id+"F1.opExtrude","SWEPT_EDGE",EDGE,{"disambiguationData":[OSD([subQ3,subQ0])]}),makeQuery(id+"F1.opExtrude","CAP_FACE",FACE,{"disambiguationData":[OSD([subQ3,subQ2,subQ1,subQ0])],"isStart":true})],"blendedInto":[makeQuery(id+"F1.opExtrude","CAP_FACE",FACE,{"disambiguationData":[OSD([subQ3,subQ2,subQ1,subQ0])],"isStart":true})]})])]});}
            var Q7;
            {var subQ0=sQuery(id+"F0.wireOp",EDGE,"E0.right");Q7=makeQuery(id+"F5.boolean.opBoolean","SPLIT",EDGE,{"disambiguationData":[TD([makeQuery(id+"F5.opExtrude","SWEPT_FACE",FACE,{"disambiguationData":[OSD([sQuery(id+"F4.wireOp",EDGE,"E3.1.6.0")])]})])],"derivedFrom":makeQuery(id+"F3.opShell","OFFSET_EDGE",EDGE,{"disambiguationData":[OSD([subQ0]),TDD([makeQuery(id+"F1.opExtrude","CAP_EDGE",EDGE,{"disambiguationData":[OSD([subQ0])],"isStart":true})])]})});}
            var Q8;
            {var subQ0=sQuery(id+"F0.wireOp",EDGE,"E0.right");var subQ1=sQuery(id+"F0.wireOp",EDGE,"E0.left");var subQ2=sQuery(id+"F0.wireOp",EDGE,"E0.top");var subQ3=sQuery(id+"F0.wireOp",EDGE,"E0.bottom");Q8=makeQuery(id+"F3.opShell","OFFSET_EDGE",EDGE,{"disambiguationData":[OSD([subQ3,subQ2,subQ1,subQ0]),TDD([makeQuery(id+"F2.opFillet","BLEND_EDGE",EDGE,{"blendedFrom":[makeQuery(id+"F1.opExtrude","SWEPT_EDGE",EDGE,{"disambiguationData":[OSD([subQ2,subQ0])]}),makeQuery(id+"F1.opExtrude","CAP_FACE",FACE,{"disambiguationData":[OSD([subQ3,subQ2,subQ1,subQ0])],"isStart":true})],"blendedInto":[makeQuery(id+"F1.opExtrude","CAP_FACE",FACE,{"disambiguationData":[OSD([subQ3,subQ2,subQ1,subQ0])],"isStart":true})]})])]});}
            fillet(context, id + "F10", {"entities" : qUnion([Q0, Q1, Q2, Q3, Q4, Q5, Q6, Q7, Q8]), "radius" : 1.5 * mm, "tangentPropagation" : true, "allowEdgeOverflow" : false});
        }
        {
            var Q0;
            {var subQ0=sQuery(id+"F0.wireOp",EDGE,"E0.left");Q0=makeQuery(id+"F5.boolean.opBoolean","SPLIT",EDGE,{"disambiguationData":[TD([makeQuery(id+"F5.opExtrude","SWEPT_FACE",FACE,{"disambiguationData":[OSD([sQuery(id+"F4.wireOp",EDGE,"E2.top")])]})])],"derivedFrom":makeQuery(id+"F3.opShell","OFFSET_EDGE",EDGE,{"disambiguationData":[OSD([subQ0]),TDD([makeQuery(id+"F1.opExtrude","CAP_EDGE",EDGE,{"disambiguationData":[OSD([subQ0])],"isStart":true})])]})});}
            var Q1;
            {var subQ0=sQuery(id+"F0.wireOp",EDGE,"E0.left");Q1=makeQuery(id+"F5.boolean.opBoolean","SPLIT",EDGE,{"disambiguationData":[TD([makeQuery(id+"F5.opExtrude","SWEPT_FACE",FACE,{"disambiguationData":[OSD([sQuery(id+"F4.wireOp",EDGE,"E3.0.1.0")])]})])],"derivedFrom":makeQuery(id+"F3.opShell","OFFSET_EDGE",EDGE,{"disambiguationData":[OSD([subQ0]),TDD([makeQuery(id+"F1.opExtrude","CAP_EDGE",EDGE,{"disambiguationData":[OSD([subQ0])],"isStart":true})])]})});}
            var Q2;
            {var subQ0=sQuery(id+"F0.wireOp",EDGE,"E0.left");Q2=makeQuery(id+"F5.boolean.opBoolean","SPLIT",EDGE,{"disambiguationData":[TD([makeQuery(id+"F5.opExtrude","SWEPT_FACE",FACE,{"disambiguationData":[OSD([sQuery(id+"F4.wireOp",EDGE,"E3.0.2.0")])]})])],"derivedFrom":makeQuery(id+"F3.opShell","OFFSET_EDGE",EDGE,{"disambiguationData":[OSD([subQ0]),TDD([makeQuery(id+"F1.opExtrude","CAP_EDGE",EDGE,{"disambiguationData":[OSD([subQ0])],"isStart":true})])]})});}
            var Q3;
            {var subQ0=sQuery(id+"F0.wireOp",EDGE,"E0.left");Q3=makeQuery(id+"F5.boolean.opBoolean","SPLIT",EDGE,{"disambiguationData":[TD([makeQuery(id+"F5.opExtrude","SWEPT_FACE",FACE,{"disambiguationData":[OSD([sQuery(id+"F4.wireOp",EDGE,"E3.0.3.0")])]})])],"derivedFrom":makeQuery(id+"F3.opShell","OFFSET_EDGE",EDGE,{"disambiguationData":[OSD([subQ0]),TDD([makeQuery(id+"F1.opExtrude","CAP_EDGE",EDGE,{"disambiguationData":[OSD([subQ0])],"isStart":true})])]})});}
            var Q4;
            {var subQ0=sQuery(id+"F0.wireOp",EDGE,"E0.left");Q4=makeQuery(id+"F5.boolean.opBoolean","SPLIT",EDGE,{"disambiguationData":[TD([makeQuery(id+"F5.opExtrude","SWEPT_FACE",FACE,{"disambiguationData":[OSD([sQuery(id+"F4.wireOp",EDGE,"E3.0.4.0")])]})])],"derivedFrom":makeQuery(id+"F3.opShell","OFFSET_EDGE",EDGE,{"disambiguationData":[OSD([subQ0]),TDD([makeQuery(id+"F1.opExtrude","CAP_EDGE",EDGE,{"disambiguationData":[OSD([subQ0])],"isStart":true})])]})});}
            var Q5;
            {var subQ0=sQuery(id+"F0.wireOp",EDGE,"E0.left");Q5=makeQuery(id+"F5.boolean.opBoolean","SPLIT",EDGE,{"disambiguationData":[TD([makeQuery(id+"F5.opExtrude","SWEPT_FACE",FACE,{"disambiguationData":[OSD([sQuery(id+"F4.wireOp",EDGE,"E3.0.5.0")])]})])],"derivedFrom":makeQuery(id+"F3.opShell","OFFSET_EDGE",EDGE,{"disambiguationData":[OSD([subQ0]),TDD([makeQuery(id+"F1.opExtrude","CAP_EDGE",EDGE,{"disambiguationData":[OSD([subQ0])],"isStart":true})])]})});}
            var Q6;
            {var subQ0=sQuery(id+"F0.wireOp",EDGE,"E0.left");Q6=makeQuery(id+"F5.boolean.opBoolean","SPLIT",EDGE,{"disambiguationData":[TD([makeQuery(id+"F5.opExtrude","SWEPT_FACE",FACE,{"disambiguationData":[OSD([sQuery(id+"F4.wireOp",EDGE,"E3.0.6.0")])]})])],"derivedFrom":makeQuery(id+"F3.opShell","OFFSET_EDGE",EDGE,{"disambiguationData":[OSD([subQ0]),TDD([makeQuery(id+"F1.opExtrude","CAP_EDGE",EDGE,{"disambiguationData":[OSD([subQ0])],"isStart":true})])]})});}
            fillet(context, id + "F11", {"entities" : qUnion([Q0, Q1, Q2, Q3, Q4, Q5, Q6]), "radius" : 1.5 * mm, "tangentPropagation" : true, "allowEdgeOverflow" : false});
        }
        {
            var Q0;
            Q0=makeQuery(id+"F6.opFillet","BLEND_EDGE",EDGE,{"blendedFrom":[makeQuery(id+"F5.opExtrude","CAP_EDGE",EDGE,{"disambiguationData":[OSD([sQuery(id+"F4.wireOp",EDGE,"E3.0.3.2")])],"isStart":false}),makeQuery(id+"F5.opExtrude","SWEPT_FACE",FACE,{"disambiguationData":[OSD([sQuery(id+"F4.wireOp",EDGE,"E3.0.3.0")])]})],"blendedInto":[makeQuery(id+"F5.opExtrude","SWEPT_FACE",FACE,{"disambiguationData":[OSD([sQuery(id+"F4.wireOp",EDGE,"E3.0.3.0")])]})]});
            var Q1;
            Q1=makeQuery(id+"F6.opFillet","BLEND_EDGE",EDGE,{"blendedFrom":[makeQuery(id+"F5.opExtrude","CAP_EDGE",EDGE,{"disambiguationData":[OSD([sQuery(id+"F4.wireOp",EDGE,"E3.0.2.2")])],"isStart":false}),makeQuery(id+"F5.opExtrude","SWEPT_FACE",FACE,{"disambiguationData":[OSD([sQuery(id+"F4.wireOp",EDGE,"E3.0.2.0")])]})],"blendedInto":[makeQuery(id+"F5.opExtrude","SWEPT_FACE",FACE,{"disambiguationData":[OSD([sQuery(id+"F4.wireOp",EDGE,"E3.0.2.0")])]})]});
            var Q2;
            Q2=makeQuery(id+"F6.opFillet","BLEND_EDGE",EDGE,{"blendedFrom":[makeQuery(id+"F5.opExtrude","CAP_EDGE",EDGE,{"disambiguationData":[OSD([sQuery(id+"F4.wireOp",EDGE,"E3.0.2.2")])],"isStart":false}),makeQuery(id+"F5.opExtrude","SWEPT_FACE",FACE,{"disambiguationData":[OSD([sQuery(id+"F4.wireOp",EDGE,"E3.0.2.1")])]})],"blendedInto":[makeQuery(id+"F5.opExtrude","SWEPT_FACE",FACE,{"disambiguationData":[OSD([sQuery(id+"F4.wireOp",EDGE,"E3.0.2.1")])]})]});
            var Q3;
            Q3=makeQuery(id+"F6.opFillet","BLEND_EDGE",EDGE,{"blendedFrom":[makeQuery(id+"F5.opExtrude","CAP_EDGE",EDGE,{"disambiguationData":[OSD([sQuery(id+"F4.wireOp",EDGE,"E3.0.1.2")])],"isStart":false}),makeQuery(id+"F5.opExtrude","SWEPT_FACE",FACE,{"disambiguationData":[OSD([sQuery(id+"F4.wireOp",EDGE,"E3.0.1.0")])]})],"blendedInto":[makeQuery(id+"F5.opExtrude","SWEPT_FACE",FACE,{"disambiguationData":[OSD([sQuery(id+"F4.wireOp",EDGE,"E3.0.1.0")])]})]});
            var Q4;
            Q4=makeQuery(id+"F6.opFillet","BLEND_EDGE",EDGE,{"blendedFrom":[makeQuery(id+"F5.opExtrude","CAP_EDGE",EDGE,{"disambiguationData":[OSD([sQuery(id+"F4.wireOp",EDGE,"E3.0.1.2")])],"isStart":false}),makeQuery(id+"F5.opExtrude","SWEPT_FACE",FACE,{"disambiguationData":[OSD([sQuery(id+"F4.wireOp",EDGE,"E3.0.1.1")])]})],"blendedInto":[makeQuery(id+"F5.opExtrude","SWEPT_FACE",FACE,{"disambiguationData":[OSD([sQuery(id+"F4.wireOp",EDGE,"E3.0.1.1")])]})]});
            var Q5;
            Q5=makeQuery(id+"F6.opFillet","BLEND_EDGE",EDGE,{"blendedFrom":[makeQuery(id+"F5.opExtrude","CAP_EDGE",EDGE,{"disambiguationData":[OSD([sQuery(id+"F4.wireOp",EDGE,"E3.0.3.2")])],"isStart":false}),makeQuery(id+"F5.opExtrude","SWEPT_FACE",FACE,{"disambiguationData":[OSD([sQuery(id+"F4.wireOp",EDGE,"E3.0.3.1")])]})],"blendedInto":[makeQuery(id+"F5.opExtrude","SWEPT_FACE",FACE,{"disambiguationData":[OSD([sQuery(id+"F4.wireOp",EDGE,"E3.0.3.1")])]})]});
            var Q6;
            Q6=makeQuery(id+"F6.opFillet","BLEND_EDGE",EDGE,{"blendedFrom":[makeQuery(id+"F5.opExtrude","CAP_EDGE",EDGE,{"disambiguationData":[OSD([sQuery(id+"F4.wireOp",EDGE,"E2.right")])],"isStart":false}),makeQuery(id+"F5.opExtrude","SWEPT_FACE",FACE,{"disambiguationData":[OSD([sQuery(id+"F4.wireOp",EDGE,"E2.top")])]})],"blendedInto":[makeQuery(id+"F5.opExtrude","SWEPT_FACE",FACE,{"disambiguationData":[OSD([sQuery(id+"F4.wireOp",EDGE,"E2.top")])]})]});
            var Q7;
            Q7=makeQuery(id+"F6.opFillet","BLEND_EDGE",EDGE,{"blendedFrom":[makeQuery(id+"F5.opExtrude","CAP_EDGE",EDGE,{"disambiguationData":[OSD([sQuery(id+"F4.wireOp",EDGE,"E2.right")])],"isStart":false}),makeQuery(id+"F5.opExtrude","SWEPT_FACE",FACE,{"disambiguationData":[OSD([sQuery(id+"F4.wireOp",EDGE,"E2.bottom")])]})],"blendedInto":[makeQuery(id+"F5.opExtrude","SWEPT_FACE",FACE,{"disambiguationData":[OSD([sQuery(id+"F4.wireOp",EDGE,"E2.bottom")])]})]});
            var Q8;
            Q8=makeQuery(id+"F6.opFillet","BLEND_EDGE",EDGE,{"blendedFrom":[makeQuery(id+"F5.opExtrude","CAP_EDGE",EDGE,{"disambiguationData":[OSD([sQuery(id+"F4.wireOp",EDGE,"E3.1.0.3")])],"isStart":false}),makeQuery(id+"F5.opExtrude","SWEPT_FACE",FACE,{"disambiguationData":[OSD([sQuery(id+"F4.wireOp",EDGE,"E3.1.0.1")])]})],"blendedInto":[makeQuery(id+"F5.opExtrude","SWEPT_FACE",FACE,{"disambiguationData":[OSD([sQuery(id+"F4.wireOp",EDGE,"E3.1.0.1")])]})]});
            var Q9;
            Q9=makeQuery(id+"F6.opFillet","BLEND_EDGE",EDGE,{"blendedFrom":[makeQuery(id+"F5.opExtrude","CAP_EDGE",EDGE,{"disambiguationData":[OSD([sQuery(id+"F4.wireOp",EDGE,"E3.1.0.3")])],"isStart":false}),makeQuery(id+"F5.opExtrude","SWEPT_FACE",FACE,{"disambiguationData":[OSD([sQuery(id+"F4.wireOp",EDGE,"E3.1.0.0")])]})],"blendedInto":[makeQuery(id+"F5.opExtrude","SWEPT_FACE",FACE,{"disambiguationData":[OSD([sQuery(id+"F4.wireOp",EDGE,"E3.1.0.0")])]})]});
            var Q10;
            Q10=makeQuery(id+"F6.opFillet","BLEND_EDGE",EDGE,{"blendedFrom":[makeQuery(id+"F5.opExtrude","CAP_EDGE",EDGE,{"disambiguationData":[OSD([sQuery(id+"F4.wireOp",EDGE,"E3.1.1.3")])],"isStart":false}),makeQuery(id+"F5.opExtrude","SWEPT_FACE",FACE,{"disambiguationData":[OSD([sQuery(id+"F4.wireOp",EDGE,"E3.1.1.1")])]})],"blendedInto":[makeQuery(id+"F5.opExtrude","SWEPT_FACE",FACE,{"disambiguationData":[OSD([sQuery(id+"F4.wireOp",EDGE,"E3.1.1.1")])]})]});
            var Q11;
            Q11=makeQuery(id+"F6.opFillet","BLEND_EDGE",EDGE,{"blendedFrom":[makeQuery(id+"F5.opExtrude","CAP_EDGE",EDGE,{"disambiguationData":[OSD([sQuery(id+"F4.wireOp",EDGE,"E3.1.2.3")])],"isStart":false}),makeQuery(id+"F5.opExtrude","SWEPT_FACE",FACE,{"disambiguationData":[OSD([sQuery(id+"F4.wireOp",EDGE,"E3.1.2.1")])]})],"blendedInto":[makeQuery(id+"F5.opExtrude","SWEPT_FACE",FACE,{"disambiguationData":[OSD([sQuery(id+"F4.wireOp",EDGE,"E3.1.2.1")])]})]});
            var Q12;
            Q12=makeQuery(id+"F6.opFillet","BLEND_EDGE",EDGE,{"blendedFrom":[makeQuery(id+"F5.opExtrude","CAP_EDGE",EDGE,{"disambiguationData":[OSD([sQuery(id+"F4.wireOp",EDGE,"E3.1.2.3")])],"isStart":false}),makeQuery(id+"F5.opExtrude","SWEPT_FACE",FACE,{"disambiguationData":[OSD([sQuery(id+"F4.wireOp",EDGE,"E3.1.2.0")])]})],"blendedInto":[makeQuery(id+"F5.opExtrude","SWEPT_FACE",FACE,{"disambiguationData":[OSD([sQuery(id+"F4.wireOp",EDGE,"E3.1.2.0")])]})]});
            var Q13;
            Q13=makeQuery(id+"F6.opFillet","BLEND_EDGE",EDGE,{"blendedFrom":[makeQuery(id+"F5.opExtrude","CAP_EDGE",EDGE,{"disambiguationData":[OSD([sQuery(id+"F4.wireOp",EDGE,"E3.1.3.3")])],"isStart":false}),makeQuery(id+"F5.opExtrude","SWEPT_FACE",FACE,{"disambiguationData":[OSD([sQuery(id+"F4.wireOp",EDGE,"E3.1.3.1")])]})],"blendedInto":[makeQuery(id+"F5.opExtrude","SWEPT_FACE",FACE,{"disambiguationData":[OSD([sQuery(id+"F4.wireOp",EDGE,"E3.1.3.1")])]})]});
            var Q14;
            Q14=makeQuery(id+"F6.opFillet","BLEND_EDGE",EDGE,{"blendedFrom":[makeQuery(id+"F5.opExtrude","CAP_EDGE",EDGE,{"disambiguationData":[OSD([sQuery(id+"F4.wireOp",EDGE,"E3.1.3.3")])],"isStart":false}),makeQuery(id+"F5.opExtrude","SWEPT_FACE",FACE,{"disambiguationData":[OSD([sQuery(id+"F4.wireOp",EDGE,"E3.1.3.0")])]})],"blendedInto":[makeQuery(id+"F5.opExtrude","SWEPT_FACE",FACE,{"disambiguationData":[OSD([sQuery(id+"F4.wireOp",EDGE,"E3.1.3.0")])]})]});
            var Q15;
            Q15=makeQuery(id+"F6.opFillet","BLEND_EDGE",EDGE,{"blendedFrom":[makeQuery(id+"F5.opExtrude","CAP_EDGE",EDGE,{"disambiguationData":[OSD([sQuery(id+"F4.wireOp",EDGE,"E3.1.4.3")])],"isStart":false}),makeQuery(id+"F5.opExtrude","SWEPT_FACE",FACE,{"disambiguationData":[OSD([sQuery(id+"F4.wireOp",EDGE,"E3.1.4.1")])]})],"blendedInto":[makeQuery(id+"F5.opExtrude","SWEPT_FACE",FACE,{"disambiguationData":[OSD([sQuery(id+"F4.wireOp",EDGE,"E3.1.4.1")])]})]});
            var Q16;
            Q16=makeQuery(id+"F6.opFillet","BLEND_EDGE",EDGE,{"blendedFrom":[makeQuery(id+"F5.opExtrude","CAP_EDGE",EDGE,{"disambiguationData":[OSD([sQuery(id+"F4.wireOp",EDGE,"E3.1.4.3")])],"isStart":false}),makeQuery(id+"F5.opExtrude","SWEPT_FACE",FACE,{"disambiguationData":[OSD([sQuery(id+"F4.wireOp",EDGE,"E3.1.4.0")])]})],"blendedInto":[makeQuery(id+"F5.opExtrude","SWEPT_FACE",FACE,{"disambiguationData":[OSD([sQuery(id+"F4.wireOp",EDGE,"E3.1.4.0")])]})]});
            var Q17;
            Q17=makeQuery(id+"F6.opFillet","BLEND_EDGE",EDGE,{"blendedFrom":[makeQuery(id+"F5.opExtrude","CAP_EDGE",EDGE,{"disambiguationData":[OSD([sQuery(id+"F4.wireOp",EDGE,"E3.1.5.3")])],"isStart":false}),makeQuery(id+"F5.opExtrude","SWEPT_FACE",FACE,{"disambiguationData":[OSD([sQuery(id+"F4.wireOp",EDGE,"E3.1.5.1")])]})],"blendedInto":[makeQuery(id+"F5.opExtrude","SWEPT_FACE",FACE,{"disambiguationData":[OSD([sQuery(id+"F4.wireOp",EDGE,"E3.1.5.1")])]})]});
            var Q18;
            Q18=makeQuery(id+"F6.opFillet","BLEND_EDGE",EDGE,{"blendedFrom":[makeQuery(id+"F5.opExtrude","CAP_EDGE",EDGE,{"disambiguationData":[OSD([sQuery(id+"F4.wireOp",EDGE,"E3.1.5.3")])],"isStart":false}),makeQuery(id+"F5.opExtrude","SWEPT_FACE",FACE,{"disambiguationData":[OSD([sQuery(id+"F4.wireOp",EDGE,"E3.1.5.0")])]})],"blendedInto":[makeQuery(id+"F5.opExtrude","SWEPT_FACE",FACE,{"disambiguationData":[OSD([sQuery(id+"F4.wireOp",EDGE,"E3.1.5.0")])]})]});
            var Q19;
            Q19=makeQuery(id+"F6.opFillet","BLEND_EDGE",EDGE,{"blendedFrom":[makeQuery(id+"F5.opExtrude","CAP_EDGE",EDGE,{"disambiguationData":[OSD([sQuery(id+"F4.wireOp",EDGE,"E3.1.6.3")])],"isStart":false}),makeQuery(id+"F5.opExtrude","SWEPT_FACE",FACE,{"disambiguationData":[OSD([sQuery(id+"F4.wireOp",EDGE,"E3.1.6.1")])]})],"blendedInto":[makeQuery(id+"F5.opExtrude","SWEPT_FACE",FACE,{"disambiguationData":[OSD([sQuery(id+"F4.wireOp",EDGE,"E3.1.6.1")])]})]});
            var Q20;
            Q20=makeQuery(id+"F6.opFillet","BLEND_EDGE",EDGE,{"blendedFrom":[makeQuery(id+"F5.opExtrude","CAP_EDGE",EDGE,{"disambiguationData":[OSD([sQuery(id+"F4.wireOp",EDGE,"E3.1.6.3")])],"isStart":false}),makeQuery(id+"F5.opExtrude","SWEPT_FACE",FACE,{"disambiguationData":[OSD([sQuery(id+"F4.wireOp",EDGE,"E3.1.6.0")])]})],"blendedInto":[makeQuery(id+"F5.opExtrude","SWEPT_FACE",FACE,{"disambiguationData":[OSD([sQuery(id+"F4.wireOp",EDGE,"E3.1.6.0")])]})]});
            var Q21;
            Q21=makeQuery(id+"F6.opFillet","BLEND_EDGE",EDGE,{"blendedFrom":[makeQuery(id+"F5.opExtrude","CAP_EDGE",EDGE,{"disambiguationData":[OSD([sQuery(id+"F4.wireOp",EDGE,"E3.1.7.3")])],"isStart":false}),makeQuery(id+"F5.opExtrude","SWEPT_FACE",FACE,{"disambiguationData":[OSD([sQuery(id+"F4.wireOp",EDGE,"E3.1.7.1")])]})],"blendedInto":[makeQuery(id+"F5.opExtrude","SWEPT_FACE",FACE,{"disambiguationData":[OSD([sQuery(id+"F4.wireOp",EDGE,"E3.1.7.1")])]})]});
            var Q22;
            Q22=makeQuery(id+"F6.opFillet","BLEND_EDGE",EDGE,{"blendedFrom":[makeQuery(id+"F5.opExtrude","CAP_EDGE",EDGE,{"disambiguationData":[OSD([sQuery(id+"F4.wireOp",EDGE,"E3.0.7.2")])],"isStart":false}),makeQuery(id+"F5.opExtrude","SWEPT_FACE",FACE,{"disambiguationData":[OSD([sQuery(id+"F4.wireOp",EDGE,"E3.0.7.0")])]})],"blendedInto":[makeQuery(id+"F5.opExtrude","SWEPT_FACE",FACE,{"disambiguationData":[OSD([sQuery(id+"F4.wireOp",EDGE,"E3.0.7.0")])]})]});
            var Q23;
            Q23=makeQuery(id+"F6.opFillet","BLEND_EDGE",EDGE,{"blendedFrom":[makeQuery(id+"F5.opExtrude","CAP_EDGE",EDGE,{"disambiguationData":[OSD([sQuery(id+"F4.wireOp",EDGE,"E3.0.6.2")])],"isStart":false}),makeQuery(id+"F5.opExtrude","SWEPT_FACE",FACE,{"disambiguationData":[OSD([sQuery(id+"F4.wireOp",EDGE,"E3.0.6.0")])]})],"blendedInto":[makeQuery(id+"F5.opExtrude","SWEPT_FACE",FACE,{"disambiguationData":[OSD([sQuery(id+"F4.wireOp",EDGE,"E3.0.6.0")])]})]});
            var Q24;
            Q24=makeQuery(id+"F6.opFillet","BLEND_EDGE",EDGE,{"blendedFrom":[makeQuery(id+"F5.opExtrude","CAP_EDGE",EDGE,{"disambiguationData":[OSD([sQuery(id+"F4.wireOp",EDGE,"E3.0.6.2")])],"isStart":false}),makeQuery(id+"F5.opExtrude","SWEPT_FACE",FACE,{"disambiguationData":[OSD([sQuery(id+"F4.wireOp",EDGE,"E3.0.6.1")])]})],"blendedInto":[makeQuery(id+"F5.opExtrude","SWEPT_FACE",FACE,{"disambiguationData":[OSD([sQuery(id+"F4.wireOp",EDGE,"E3.0.6.1")])]})]});
            var Q25;
            Q25=makeQuery(id+"F6.opFillet","BLEND_EDGE",EDGE,{"blendedFrom":[makeQuery(id+"F5.opExtrude","CAP_EDGE",EDGE,{"disambiguationData":[OSD([sQuery(id+"F4.wireOp",EDGE,"E3.0.7.2")])],"isStart":false}),makeQuery(id+"F5.opExtrude","SWEPT_FACE",FACE,{"disambiguationData":[OSD([sQuery(id+"F4.wireOp",EDGE,"E3.0.7.1")])]})],"blendedInto":[makeQuery(id+"F5.opExtrude","SWEPT_FACE",FACE,{"disambiguationData":[OSD([sQuery(id+"F4.wireOp",EDGE,"E3.0.7.1")])]})]});
            var Q26;
            Q26=makeQuery(id+"F6.opFillet","BLEND_EDGE",EDGE,{"blendedFrom":[makeQuery(id+"F5.opExtrude","CAP_EDGE",EDGE,{"disambiguationData":[OSD([sQuery(id+"F4.wireOp",EDGE,"E3.0.5.2")])],"isStart":false}),makeQuery(id+"F5.opExtrude","SWEPT_FACE",FACE,{"disambiguationData":[OSD([sQuery(id+"F4.wireOp",EDGE,"E3.0.5.0")])]})],"blendedInto":[makeQuery(id+"F5.opExtrude","SWEPT_FACE",FACE,{"disambiguationData":[OSD([sQuery(id+"F4.wireOp",EDGE,"E3.0.5.0")])]})]});
            var Q27;
            Q27=makeQuery(id+"F6.opFillet","BLEND_EDGE",EDGE,{"blendedFrom":[makeQuery(id+"F5.opExtrude","CAP_EDGE",EDGE,{"disambiguationData":[OSD([sQuery(id+"F4.wireOp",EDGE,"E3.0.4.2")])],"isStart":false}),makeQuery(id+"F5.opExtrude","SWEPT_FACE",FACE,{"disambiguationData":[OSD([sQuery(id+"F4.wireOp",EDGE,"E3.0.4.0")])]})],"blendedInto":[makeQuery(id+"F5.opExtrude","SWEPT_FACE",FACE,{"disambiguationData":[OSD([sQuery(id+"F4.wireOp",EDGE,"E3.0.4.0")])]})]});
            var Q28;
            Q28=makeQuery(id+"F6.opFillet","BLEND_EDGE",EDGE,{"blendedFrom":[makeQuery(id+"F5.opExtrude","CAP_EDGE",EDGE,{"disambiguationData":[OSD([sQuery(id+"F4.wireOp",EDGE,"E3.0.5.2")])],"isStart":false}),makeQuery(id+"F5.opExtrude","SWEPT_FACE",FACE,{"disambiguationData":[OSD([sQuery(id+"F4.wireOp",EDGE,"E3.0.5.1")])]})],"blendedInto":[makeQuery(id+"F5.opExtrude","SWEPT_FACE",FACE,{"disambiguationData":[OSD([sQuery(id+"F4.wireOp",EDGE,"E3.0.5.1")])]})]});
            var Q29;
            Q29=makeQuery(id+"F6.opFillet","BLEND_EDGE",EDGE,{"blendedFrom":[makeQuery(id+"F5.opExtrude","CAP_EDGE",EDGE,{"disambiguationData":[OSD([sQuery(id+"F4.wireOp",EDGE,"E3.0.4.2")])],"isStart":false}),makeQuery(id+"F5.opExtrude","SWEPT_FACE",FACE,{"disambiguationData":[OSD([sQuery(id+"F4.wireOp",EDGE,"E3.0.4.1")])]})],"blendedInto":[makeQuery(id+"F5.opExtrude","SWEPT_FACE",FACE,{"disambiguationData":[OSD([sQuery(id+"F4.wireOp",EDGE,"E3.0.4.1")])]})]});
            var Q30;
            {var subQ0=sQuery(id+"F0.wireOp",EDGE,"E0.left");Q30=makeQuery(id+"F3.opShell","OFFSET_EDGE",EDGE,{"disambiguationData":[OSD([subQ0]),TDD([makeQuery(id+"F1.opExtrude","CAP_EDGE",EDGE,{"disambiguationData":[OSD([subQ0])],"isStart":false})])]});}
            fillet(context, id + "F12", {"entities" : qUnion([Q0, Q1, Q2, Q3, Q4, Q5, Q6, Q7, Q8, Q9, Q10, Q11, Q12, Q13, Q14, Q15, Q16, Q17, Q18, Q19, Q20, Q21, Q22, Q23, Q24, Q25, Q26, Q27, Q28, Q29, Q30]), "radius" : .75 * mm, "tangentPropagation" : true, "allowEdgeOverflow" : false});
        }
        {
            var Q0;
            Q0=qCreatedBy(makeId("Top.planeOp"),FACE);
            var sketch = newSketch(context, id + "F13", { "sketchPlane" : qUnion([Q0])});
            skLineSegment(sketch, "E8.bottom", {"start": v(0, 43) * mm, "end": v(11, 43) * mm});
            skLineSegment(sketch, "E8.top", {"start": v(0, -43) * mm, "end": v(11, -43) * mm});
            skLineSegment(sketch, "E8.left", {"start": v(0, 43) * mm, "end": v(0, -43) * mm});
            skLineSegment(sketch, "E8.right", {"start": v(19, 35) * mm, "end": v(19, -35) * mm});
            skPoint(sketch, "E9.visualSharp", {"position": v(19, 43) * mm});
            skArc(sketch, "E9.filletArc", {"start": v(19, 35) * mm, "mid": v(16.66, 40.66) * mm, "end": v(11, 43) * mm});
            skPoint(sketch, "E10.visualSharp", {"position": v(19, -43) * mm});
            skArc(sketch, "E10.filletArc", {"start": v(11, -43) * mm, "mid": v(16.66, -40.66) * mm, "end": v(19, -35) * mm});
            skLineSegment(sketch, "E11.0", {"start": v(0, -44.5) * mm, "end": v(11, -44.5) * mm});
            skLineSegment(sketch, "E11.1", {"start": v(0, 44.5) * mm, "end": v(11, 44.5) * mm});
            skArc(sketch, "E11.2", {"start": v(20.5, 35) * mm, "mid": v(17.72, 41.72) * mm, "end": v(11, 44.5) * mm});
            skLineSegment(sketch, "E11.3", {"start": v(20.5, 35) * mm, "end": v(20.5, -35) * mm});
            skArc(sketch, "E11.4", {"start": v(11, -44.5) * mm, "mid": v(17.72, -41.72) * mm, "end": v(20.5, -35) * mm});
            skSolve(sketch);
        }
        {
            var Q0;
            Q0=qCreatedBy(makeId("Top.planeOp"),FACE);
            cPlane(context, id + "F14", {"entities" : qUnion([Q0]), "cplaneType" : CPlaneType.OFFSET, "offset" : 5 * mm, "width" : 150 * mm, "height" : 150 * mm});
        }
        {
            var Q0;
            Q0=qCreatedBy(id+"F14.planeOp",FACE);
            var sketch = newSketch(context, id + "F15", { "sketchPlane" : qUnion([Q0])});
            skLineSegment(sketch, "E12.0", {"start": v(0, 43) * mm, "end": v(11, 43) * mm});
            skLineSegment(sketch, "E12.1", {"start": v(0, -43) * mm, "end": v(11, -43) * mm});
            skLineSegment(sketch, "E12.2", {"start": v(0, 43) * mm, "end": v(0, -43) * mm});
            skLineSegment(sketch, "E12.3", {"start": v(19, 35) * mm, "end": v(19, -35) * mm});
            skPoint(sketch, "E12.4", {"position": v(19, 43) * mm});
            skArc(sketch, "E12.5", {"start": v(19, 35) * mm, "mid": v(16.66, 40.66) * mm, "end": v(11, 43) * mm});
            skPoint(sketch, "E12.6", {"position": v(19, -43) * mm});
            skArc(sketch, "E12.7", {"start": v(11, -43) * mm, "mid": v(16.66, -40.66) * mm, "end": v(19, -35) * mm});
            skLineSegment(sketch, "E12.8", {"start": v(0, -44.5) * mm, "end": v(11, -44.5) * mm});
            skLineSegment(sketch, "E12.9", {"start": v(0, 44.5) * mm, "end": v(11, 44.5) * mm});
            skArc(sketch, "E12.10", {"start": v(20.5, 35) * mm, "mid": v(17.72, 41.72) * mm, "end": v(11, 44.5) * mm});
            skLineSegment(sketch, "E12.11", {"start": v(20.5, 35) * mm, "end": v(20.5, -35) * mm});
            skArc(sketch, "E12.12", {"start": v(11, -44.5) * mm, "mid": v(17.72, -41.72) * mm, "end": v(20.5, -35) * mm});
            skLineSegment(sketch, "E13", {"start": v(0, -44.5) * mm, "end": v(-2, -44.5) * mm});
            skLineSegment(sketch, "E14", {"start": v(-2, -44.5) * mm, "end": v(-2, -43) * mm});
            skLineSegment(sketch, "E15", {"start": v(-2, -43) * mm, "end": v(0, -43) * mm});
            skLineSegment(sketch, "E16", {"start": v(0, 43) * mm, "end": v(-2, 43) * mm});
            skLineSegment(sketch, "E17", {"start": v(-2, 43) * mm, "end": v(-2, 44.5) * mm});
            skLineSegment(sketch, "E18", {"start": v(-2, 44.5) * mm, "end": v(0, 44.5) * mm});
            skSolve(sketch);
        }
        {
            var Q0;
            Q0=makeQuery(id+"F15.imprint","IMPRINT",FACE,{"disambiguationData":[TD([[makeQuery(id+"F15.imprint","IMPRINT",EDGE,{"derivedFrom":sQuery(id+"F15.wireOp",EDGE,"E12.0")}),1.0]])]});
            extrude(context, id + "F16", {"entities" : qUnion([Q0]), "depth" : 7 * mm});
        }
        {
            var Q0;
            Q0=makeQuery(id+"F16.opExtrude","SWEPT_FACE",FACE,{"disambiguationData":[OSD([sQuery(id+"F15.wireOp",EDGE,"E12.9"),sQuery(id+"F15.wireOp",EDGE,"E18")])]});
            var sketch = newSketch(context, id + "F17", { "sketchPlane" : qUnion([Q0])});
            skCircle(sketch, "E19", {"center": v(0, 8.5) * mm, "radius": 1.5 * mm});
            skSolve(sketch);
        }
        {
            var Q0;
            Q0=makeQuery(id+"F16.opExtrude","CAP_EDGE",EDGE,{"disambiguationData":[OSD([sQuery(id+"F15.wireOp",EDGE,"E14")])],"isStart":false});
            var Q1;
            Q1=makeQuery(id+"F16.opExtrude","CAP_EDGE",EDGE,{"disambiguationData":[OSD([sQuery(id+"F15.wireOp",EDGE,"E14")])],"isStart":true});
            var Q2;
            Q2=makeQuery(id+"F16.opExtrude","CAP_EDGE",EDGE,{"disambiguationData":[OSD([sQuery(id+"F15.wireOp",EDGE,"E17")])],"isStart":false});
            var Q3;
            Q3=makeQuery(id+"F16.opExtrude","CAP_EDGE",EDGE,{"disambiguationData":[OSD([sQuery(id+"F15.wireOp",EDGE,"E17")])],"isStart":true});
            fillet(context, id + "F18", {"entities" : qUnion([Q0, Q1, Q2, Q3]), "radius" : 3 * mm, "tangentPropagation" : true, "allowEdgeOverflow" : false});
        }
        {
            var Q0;
            Q0=makeQuery(id+"F16.opExtrude","CAP_EDGE",EDGE,{"disambiguationData":[OSD([sQuery(id+"F15.wireOp",EDGE,"E12.3")])],"isStart":false});
            fillet(context, id + "F19", {"entities" : qUnion([Q0]), "radius" : .75 * mm, "tangentPropagation" : true, "allowEdgeOverflow" : false});
        }
        {
            var Q0;
            Q0 = qSketchRegion(id + "F17", true);
            extrude(context, id + "F20", {"entities" : qUnion([Q0]), "operationType" : NewBodyOperationType.REMOVE, "oppositeDirection" : true, "depth" : 100 * mm});
        }
        {
            var Q0;
            Q0=makeQuery(id+"F16.opExtrude","SWEPT_FACE",FACE,{"disambiguationData":[OSD([sQuery(id+"F15.wireOp",EDGE,"E12.8"),sQuery(id+"F15.wireOp",EDGE,"E13")])]});
            var sketch = newSketch(context, id + "F21", { "sketchPlane" : qUnion([Q0])});
            skCircle(sketch, "E20", {"center": v(0, 8.5) * mm, "radius": 1.52 * mm});
            skSolve(sketch);
        }
        {
            var Q0;
            Q0 = qSketchRegion(id + "F21", true);
            extrude(context, id + "F22", {"entities" : qUnion([Q0]), "operationType" : NewBodyOperationType.ADD, "oppositeDirection" : true, "depth" : 1.5 * mm});
        }
        {
            var Q0;
            Q0=makeQuery(id+"F22.boolean.opBoolean","MERGE",FACE,{"derivedFrom":[makeQuery(id+"F16.opExtrude","SWEPT_FACE",FACE,{"disambiguationData":[OSD([sQuery(id+"F15.wireOp",EDGE,"E12.1"),sQuery(id+"F15.wireOp",EDGE,"E15")])]}),makeQuery(id+"F22.opExtrude","CAP_FACE",FACE,{"disambiguationData":[OSD([sQuery(id+"F21.wireOp",EDGE,"E20")])],"isStart":false})]});
            var sketch = newSketch(context, id + "F23", { "sketchPlane" : qUnion([Q0])});
            skCircle(sketch, "E21", {"center": v(0, 8.5) * mm, "radius": 1.25 * mm});
            skSolve(sketch);
        }
        {
            var Q0;
            Q0 = qSketchRegion(id + "F23", true);
            extrude(context, id + "F24", {"entities" : qUnion([Q0]), "operationType" : NewBodyOperationType.ADD, "depth" : 3 * mm});
        }
        {
            var Q0;
            Q0=makeQuery(id+"F16.opExtrude","SWEPT_FACE",FACE,{"disambiguationData":[OSD([sQuery(id+"F15.wireOp",EDGE,"E12.9"),sQuery(id+"F15.wireOp",EDGE,"E18")])]});
            var sketch = newSketch(context, id + "F25", { "sketchPlane" : qUnion([Q0])});
            skCircle(sketch, "E22", {"center": v(0, 8.5) * mm, "radius": 1.5 * mm});
            skSolve(sketch);
        }
        {
            var Q0;
            Q0 = qSketchRegion(id + "F25", true);
            extrude(context, id + "F26", {"entities" : qUnion([Q0]), "operationType" : NewBodyOperationType.ADD, "oppositeDirection" : true, "depth" : 1.5 * mm});
        }
        {
            var Q0;
            Q0=makeQuery(id+"F26.boolean.opBoolean","MERGE",FACE,{"derivedFrom":[makeQuery(id+"F16.opExtrude","SWEPT_FACE",FACE,{"disambiguationData":[OSD([sQuery(id+"F15.wireOp",EDGE,"E12.0"),sQuery(id+"F15.wireOp",EDGE,"E16")])]}),makeQuery(id+"F26.opExtrude","CAP_FACE",FACE,{"disambiguationData":[OSD([sQuery(id+"F25.wireOp",EDGE,"E22")])],"isStart":false})]});
            var sketch = newSketch(context, id + "F27", { "sketchPlane" : qUnion([Q0])});
            skCircle(sketch, "E23", {"center": v(0, 8.5) * mm, "radius": 1.25 * mm});
            skSolve(sketch);
        }
        {
            var Q0;
            Q0 = qSketchRegion(id + "F27", true);
            extrude(context, id + "F28", {"entities" : qUnion([Q0]), "operationType" : NewBodyOperationType.ADD, "depth" : 3 * mm});
        }
    });
